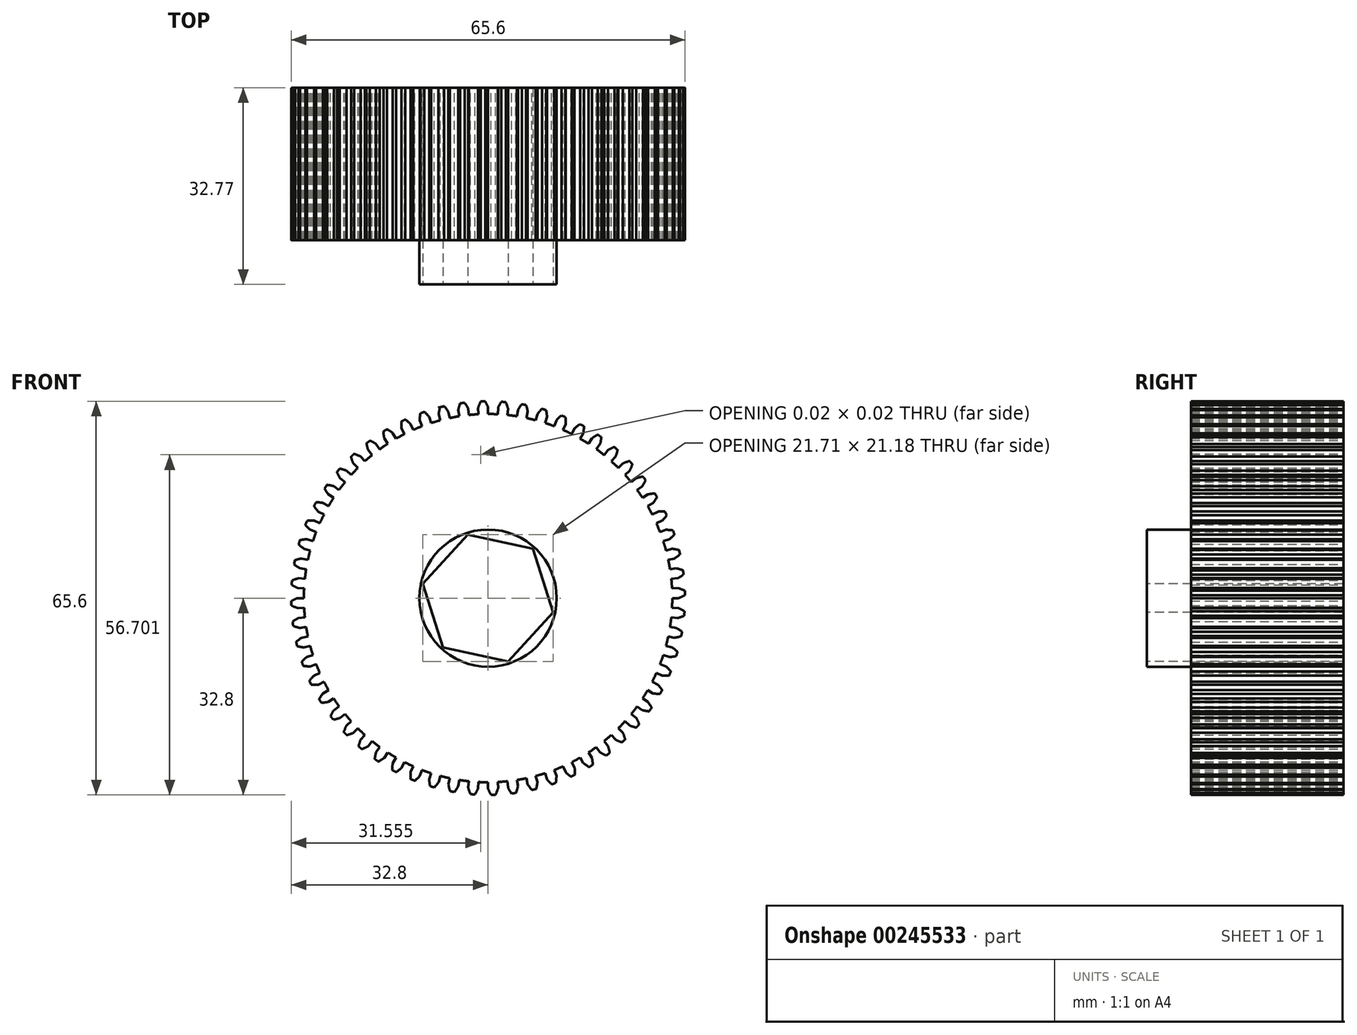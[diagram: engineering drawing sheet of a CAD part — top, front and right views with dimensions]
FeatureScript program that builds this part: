
annotation { "Feature Type Name" : "Feature", "Feature Type Description" : "" }
export const myFeature = defineFeature(function(context is Context, id is Id, definition is map)
    precondition{}
    {
        {
            var Q0;
            Q0=qCreatedBy(makeId("Front.planeOp"),FACE);
            var sketch = newSketch(context, id + "F0", { "sketchPlane" : qUnion([Q0])});
            skArc(sketch, "E0", {"start": v(-0.5, 32.8) * mm, "mid": v(-0.68, 32.8) * mm, "end": v(-0.86, 32.8) * mm});
            skLineSegment(sketch, "E1", {"start": v(0, 30.7) * mm, "end": v(0, 31.75) * mm});
            skLineSegment(sketch, "E2", {"start": v(-1.25, 23.9) * mm, "end": v(-1.25, 23.91) * mm});
            skArc(sketch, "E3", {"start": v(0, 31.75) * mm, "mid": v(-0.23, 32.28) * mm, "end": v(-0.5, 32.8) * mm});
            skArc(sketch, "E4.trimOffspring", {"start": v(-7.94, 31.83) * mm, "mid": v(-7.94, 31.79) * mm, "end": v(-7.94, 31.75) * mm});
            skArc(sketch, "E5.trimOffspring", {"start": v(-1.25, 23.91) * mm, "mid": v(-1.24, 23.91) * mm, "end": v(-1.24, 23.9) * mm});
            skLineSegment(sketch, "E6.trimOffspring", {"start": v(-0.83, 31.74) * mm, "end": v(-0.83, 31.75) * mm});
            skArc(sketch, "E7.trimOffspring", {"start": v(-1.25, 23.9) * mm, "mid": v(-1.24, 23.9) * mm, "end": v(-1.24, 23.9) * mm});
            skLineSegment(sketch, "E8.trimOffspring", {"start": v(-7.94, 31.75) * mm, "end": v(-8.25, 31.75) * mm});
            skArc(sketch, "E9.trimOffspring", {"start": v(-7.94, 31.83) * mm, "mid": v(-8.1, 31.8) * mm, "end": v(-8.25, 31.75) * mm});
            skPoint(sketch, "E10.trimOffspring.end.orphan", {"position": v(0, 60.25) * mm});
            skPoint(sketch, "E11.trimOffspring.end.orphan", {"position": v(-3.16, 60.25) * mm});
            skCircle(sketch, "E12", {"center": v(0, 0) * mm, "radius": 30.7 * mm});
            skLineSegment(sketch, "E13", {"start": v(0, 0) * mm, "end": v(-0.86, 32.8) * mm, "construction": true});
            skArc(sketch, "E14.MirrorCS", {"start": v(-1.66, 31.7) * mm, "mid": v(-1.46, 32.25) * mm, "end": v(-1.22, 32.78) * mm});
            skArc(sketch, "E15.MirrorCS", {"start": v(-1.22, 32.78) * mm, "mid": v(-1.04, 32.79) * mm, "end": v(-0.86, 32.8) * mm});
            skLineSegment(sketch, "E16.MirrorCS", {"start": v(-1.6, 30.65) * mm, "end": v(-1.66, 31.7) * mm});
            skLineSegment(sketch, "E17.1.0", {"start": v(-3.2, 30.52) * mm, "end": v(-3.32, 31.58) * mm});
            skArc(sketch, "E17.1.1", {"start": v(-3.32, 31.58) * mm, "mid": v(-3.6, 32.08) * mm, "end": v(-3.92, 32.57) * mm});
            skArc(sketch, "E17.1.2", {"start": v(-3.92, 32.57) * mm, "mid": v(-4.1, 32.55) * mm, "end": v(-4.28, 32.52) * mm});
            skArc(sketch, "E17.1.3", {"start": v(-4.64, 32.47) * mm, "mid": v(-4.46, 32.5) * mm, "end": v(-4.28, 32.52) * mm});
            skArc(sketch, "E17.1.4", {"start": v(-4.97, 31.36) * mm, "mid": v(-4.82, 31.92) * mm, "end": v(-4.64, 32.47) * mm});
            skLineSegment(sketch, "E17.1.5", {"start": v(-4.8, 30.31) * mm, "end": v(-4.97, 31.36) * mm});
            skLineSegment(sketch, "E17.2.0", {"start": v(-6.38, 30.02) * mm, "end": v(-6.6, 31.06) * mm});
            skArc(sketch, "E17.2.1", {"start": v(-6.6, 31.06) * mm, "mid": v(-6.94, 31.53) * mm, "end": v(-7.3, 31.98) * mm});
            skArc(sketch, "E17.2.2", {"start": v(-7.3, 31.98) * mm, "mid": v(-7.48, 31.94) * mm, "end": v(-7.66, 31.9) * mm});
            skArc(sketch, "E17.2.3", {"start": v(-8.01, 31.81) * mm, "mid": v(-7.83, 31.85) * mm, "end": v(-7.66, 31.9) * mm});
            skArc(sketch, "E17.2.4", {"start": v(-8.22, 30.67) * mm, "mid": v(-8.14, 31.24) * mm, "end": v(-8.01, 31.81) * mm});
            skLineSegment(sketch, "E17.2.5", {"start": v(-7.94, 29.65) * mm, "end": v(-8.22, 30.67) * mm});
            skLineSegment(sketch, "E17.3.0", {"start": v(-9.48, 29.19) * mm, "end": v(-9.81, 30.2) * mm});
            skArc(sketch, "E17.3.1", {"start": v(-9.81, 30.2) * mm, "mid": v(-10.2, 30.63) * mm, "end": v(-10.6, 31.04) * mm});
            skArc(sketch, "E17.3.2", {"start": v(-10.6, 31.04) * mm, "mid": v(-10.78, 30.98) * mm, "end": v(-10.95, 30.92) * mm});
            skArc(sketch, "E17.3.3", {"start": v(-11.3, 30.8) * mm, "mid": v(-11.12, 30.86) * mm, "end": v(-10.95, 30.92) * mm});
            skArc(sketch, "E17.3.4", {"start": v(-11.38, 29.64) * mm, "mid": v(-11.36, 30.22) * mm, "end": v(-11.3, 30.8) * mm});
            skLineSegment(sketch, "E17.3.5", {"start": v(-11, 28.65) * mm, "end": v(-11.38, 29.64) * mm});
            skLineSegment(sketch, "E17.4.0", {"start": v(-12.48, 28.04) * mm, "end": v(-12.91, 29) * mm});
            skArc(sketch, "E17.4.1", {"start": v(-12.91, 29) * mm, "mid": v(-13.34, 29.4) * mm, "end": v(-13.8, 29.76) * mm});
            skArc(sketch, "E17.4.2", {"start": v(-13.8, 29.76) * mm, "mid": v(-13.96, 29.69) * mm, "end": v(-14.12, 29.6) * mm});
            skArc(sketch, "E17.4.3", {"start": v(-14.45, 29.45) * mm, "mid": v(-14.29, 29.53) * mm, "end": v(-14.12, 29.6) * mm});
            skArc(sketch, "E17.4.4", {"start": v(-14.41, 28.29) * mm, "mid": v(-14.45, 28.87) * mm, "end": v(-14.45, 29.45) * mm});
            skLineSegment(sketch, "E17.4.5", {"start": v(-13.93, 27.35) * mm, "end": v(-14.41, 28.29) * mm});
            skLineSegment(sketch, "E17.5.0", {"start": v(-15.35, 26.58) * mm, "end": v(-15.87, 27.5) * mm});
            skArc(sketch, "E17.5.1", {"start": v(-15.88, 27.5) * mm, "mid": v(-16.34, 27.84) * mm, "end": v(-16.83, 28.16) * mm});
            skArc(sketch, "E17.5.2", {"start": v(-16.83, 28.16) * mm, "mid": v(-16.98, 28.06) * mm, "end": v(-17.14, 27.97) * mm});
            skArc(sketch, "E17.5.3", {"start": v(-17.45, 27.78) * mm, "mid": v(-17.3, 27.87) * mm, "end": v(-17.14, 27.97) * mm});
            skArc(sketch, "E17.5.4", {"start": v(-17.3, 26.63) * mm, "mid": v(-17.4, 27.2) * mm, "end": v(-17.45, 27.78) * mm});
            skLineSegment(sketch, "E17.5.5", {"start": v(-16.72, 25.74) * mm, "end": v(-17.3, 26.63) * mm});
            skLineSegment(sketch, "E17.6.0", {"start": v(-18.04, 24.83) * mm, "end": v(-18.66, 25.69) * mm});
            skArc(sketch, "E17.6.1", {"start": v(-18.66, 25.69) * mm, "mid": v(-19.16, 25.98) * mm, "end": v(-19.68, 26.25) * mm});
            skArc(sketch, "E17.6.2", {"start": v(-19.68, 26.25) * mm, "mid": v(-19.83, 26.14) * mm, "end": v(-19.97, 26.03) * mm});
            skArc(sketch, "E17.6.3", {"start": v(-20.26, 25.8) * mm, "mid": v(-20.11, 25.91) * mm, "end": v(-19.97, 26.03) * mm});
            skArc(sketch, "E17.6.4", {"start": v(-19.98, 24.67) * mm, "mid": v(-20.14, 25.23) * mm, "end": v(-20.26, 25.8) * mm});
            skLineSegment(sketch, "E17.6.5", {"start": v(-19.31, 23.85) * mm, "end": v(-19.98, 24.67) * mm});
            skLineSegment(sketch, "E17.7.0", {"start": v(-20.54, 22.8) * mm, "end": v(-21.24, 23.6) * mm});
            skArc(sketch, "E17.7.1", {"start": v(-21.24, 23.6) * mm, "mid": v(-21.77, 23.84) * mm, "end": v(-22.32, 24.04) * mm});
            skArc(sketch, "E17.7.2", {"start": v(-22.32, 24.04) * mm, "mid": v(-22.45, 23.92) * mm, "end": v(-22.58, 23.8) * mm});
            skArc(sketch, "E17.7.3", {"start": v(-22.84, 23.54) * mm, "mid": v(-22.71, 23.67) * mm, "end": v(-22.58, 23.8) * mm});
            skArc(sketch, "E17.7.4", {"start": v(-22.45, 22.45) * mm, "mid": v(-22.67, 22.99) * mm, "end": v(-22.84, 23.54) * mm});
            skLineSegment(sketch, "E17.7.5", {"start": v(-21.7, 21.7) * mm, "end": v(-22.45, 22.45) * mm});
            skLineSegment(sketch, "E17.8.0", {"start": v(-22.8, 20.54) * mm, "end": v(-23.6, 21.24) * mm});
            skArc(sketch, "E17.8.1", {"start": v(-23.6, 21.24) * mm, "mid": v(-24.14, 21.43) * mm, "end": v(-24.7, 21.58) * mm});
            skArc(sketch, "E17.8.2", {"start": v(-24.7, 21.58) * mm, "mid": v(-24.83, 21.44) * mm, "end": v(-24.94, 21.3) * mm});
            skArc(sketch, "E17.8.3", {"start": v(-25.18, 21.03) * mm, "mid": v(-25.06, 21.17) * mm, "end": v(-24.94, 21.3) * mm});
            skArc(sketch, "E17.8.4", {"start": v(-24.67, 19.98) * mm, "mid": v(-24.95, 20.5) * mm, "end": v(-25.18, 21.03) * mm});
            skLineSegment(sketch, "E17.8.5", {"start": v(-23.85, 19.31) * mm, "end": v(-24.67, 19.98) * mm});
            skLineSegment(sketch, "E17.9.0", {"start": v(-24.83, 18.04) * mm, "end": v(-25.69, 18.66) * mm});
            skArc(sketch, "E17.9.1", {"start": v(-25.69, 18.66) * mm, "mid": v(-26.25, 18.8) * mm, "end": v(-26.83, 18.88) * mm});
            skArc(sketch, "E17.9.2", {"start": v(-26.83, 18.88) * mm, "mid": v(-26.93, 18.73) * mm, "end": v(-27.03, 18.58) * mm});
            skArc(sketch, "E17.9.3", {"start": v(-27.24, 18.28) * mm, "mid": v(-27.14, 18.43) * mm, "end": v(-27.03, 18.58) * mm});
            skArc(sketch, "E17.9.4", {"start": v(-26.63, 17.3) * mm, "mid": v(-26.95, 17.77) * mm, "end": v(-27.24, 18.28) * mm});
            skLineSegment(sketch, "E17.9.5", {"start": v(-25.74, 16.72) * mm, "end": v(-26.63, 17.3) * mm});
            skLineSegment(sketch, "E17.10.0", {"start": v(-26.58, 15.35) * mm, "end": v(-27.5, 15.88) * mm});
            skArc(sketch, "E17.10.1", {"start": v(-27.5, 15.88) * mm, "mid": v(-28.07, 15.94) * mm, "end": v(-28.65, 15.97) * mm});
            skArc(sketch, "E17.10.2", {"start": v(-28.65, 15.97) * mm, "mid": v(-28.74, 15.81) * mm, "end": v(-28.83, 15.65) * mm});
            skArc(sketch, "E17.10.3", {"start": v(-29, 15.33) * mm, "mid": v(-28.92, 15.5) * mm, "end": v(-28.83, 15.65) * mm});
            skArc(sketch, "E17.10.4", {"start": v(-28.29, 14.41) * mm, "mid": v(-28.66, 14.86) * mm, "end": v(-29, 15.33) * mm});
            skLineSegment(sketch, "E17.10.5", {"start": v(-27.35, 13.93) * mm, "end": v(-28.29, 14.41) * mm});
            skLineSegment(sketch, "E17.11.0", {"start": v(-28.04, 12.48) * mm, "end": v(-29, 12.91) * mm});
            skArc(sketch, "E17.11.1", {"start": v(-29, 12.91) * mm, "mid": v(-29.59, 12.92) * mm, "end": v(-30.17, 12.89) * mm});
            skArc(sketch, "E17.11.2", {"start": v(-30.17, 12.89) * mm, "mid": v(-30.24, 12.72) * mm, "end": v(-30.3, 12.55) * mm});
            skArc(sketch, "E17.11.3", {"start": v(-30.44, 12.22) * mm, "mid": v(-30.38, 12.39) * mm, "end": v(-30.3, 12.55) * mm});
            skArc(sketch, "E17.11.4", {"start": v(-29.64, 11.38) * mm, "mid": v(-30.06, 11.78) * mm, "end": v(-30.44, 12.22) * mm});
            skLineSegment(sketch, "E17.11.5", {"start": v(-28.65, 11) * mm, "end": v(-29.64, 11.38) * mm});
            skLineSegment(sketch, "E17.12.0", {"start": v(-29.19, 9.48) * mm, "end": v(-30.2, 9.81) * mm});
            skArc(sketch, "E17.12.1", {"start": v(-30.2, 9.81) * mm, "mid": v(-30.77, 9.76) * mm, "end": v(-31.35, 9.67) * mm});
            skArc(sketch, "E17.12.2", {"start": v(-31.35, 9.67) * mm, "mid": v(-31.4, 9.5) * mm, "end": v(-31.45, 9.32) * mm});
            skArc(sketch, "E17.12.3", {"start": v(-31.55, 8.97) * mm, "mid": v(-31.5, 9.14) * mm, "end": v(-31.45, 9.32) * mm});
            skArc(sketch, "E17.12.4", {"start": v(-30.67, 8.22) * mm, "mid": v(-31.13, 8.58) * mm, "end": v(-31.55, 8.97) * mm});
            skLineSegment(sketch, "E17.12.5", {"start": v(-29.65, 7.94) * mm, "end": v(-30.67, 8.22) * mm});
            skLineSegment(sketch, "E17.13.0", {"start": v(-30.02, 6.38) * mm, "end": v(-31.06, 6.6) * mm});
            skArc(sketch, "E17.13.1", {"start": v(-31.06, 6.6) * mm, "mid": v(-31.63, 6.49) * mm, "end": v(-32.19, 6.34) * mm});
            skArc(sketch, "E17.13.2", {"start": v(-32.19, 6.34) * mm, "mid": v(-32.22, 6.16) * mm, "end": v(-32.25, 5.98) * mm});
            skArc(sketch, "E17.13.3", {"start": v(-32.32, 5.62) * mm, "mid": v(-32.29, 5.8) * mm, "end": v(-32.25, 5.98) * mm});
            skArc(sketch, "E17.13.4", {"start": v(-31.36, 4.97) * mm, "mid": v(-31.85, 5.28) * mm, "end": v(-32.32, 5.62) * mm});
            skLineSegment(sketch, "E17.13.5", {"start": v(-30.31, 4.8) * mm, "end": v(-31.36, 4.97) * mm});
            skLineSegment(sketch, "E17.14.0", {"start": v(-30.52, 3.2) * mm, "end": v(-31.58, 3.32) * mm});
            skArc(sketch, "E17.14.1", {"start": v(-31.58, 3.32) * mm, "mid": v(-32.13, 3.15) * mm, "end": v(-32.67, 2.94) * mm});
            skArc(sketch, "E17.14.2", {"start": v(-32.67, 2.94) * mm, "mid": v(-32.69, 2.76) * mm, "end": v(-32.7, 2.57) * mm});
            skArc(sketch, "E17.14.3", {"start": v(-32.73, 2.21) * mm, "mid": v(-32.72, 2.4) * mm, "end": v(-32.7, 2.57) * mm});
            skArc(sketch, "E17.14.4", {"start": v(-31.7, 1.66) * mm, "mid": v(-32.23, 1.92) * mm, "end": v(-32.73, 2.21) * mm});
            skLineSegment(sketch, "E17.14.5", {"start": v(-30.65, 1.6) * mm, "end": v(-31.7, 1.66) * mm});
            skLineSegment(sketch, "E17.15.0", {"start": v(-30.7, 0) * mm, "end": v(-31.75, 0) * mm});
            skArc(sketch, "E17.15.1", {"start": v(-31.75, 0) * mm, "mid": v(-32.28, -0.23) * mm, "end": v(-32.8, -0.5) * mm});
            skArc(sketch, "E17.15.2", {"start": v(-32.8, -0.5) * mm, "mid": v(-32.8, -0.68) * mm, "end": v(-32.8, -0.86) * mm});
            skArc(sketch, "E17.15.3", {"start": v(-32.78, -1.22) * mm, "mid": v(-32.79, -1.04) * mm, "end": v(-32.8, -0.86) * mm});
            skArc(sketch, "E17.15.4", {"start": v(-31.7, -1.66) * mm, "mid": v(-32.25, -1.46) * mm, "end": v(-32.78, -1.22) * mm});
            skLineSegment(sketch, "E17.15.5", {"start": v(-30.65, -1.6) * mm, "end": v(-31.7, -1.66) * mm});
            skLineSegment(sketch, "E17.16.0", {"start": v(-30.52, -3.2) * mm, "end": v(-31.58, -3.32) * mm});
            skArc(sketch, "E17.16.1", {"start": v(-31.58, -3.32) * mm, "mid": v(-32.08, -3.6) * mm, "end": v(-32.57, -3.92) * mm});
            skArc(sketch, "E17.16.2", {"start": v(-32.57, -3.92) * mm, "mid": v(-32.55, -4.1) * mm, "end": v(-32.52, -4.28) * mm});
            skArc(sketch, "E17.16.3", {"start": v(-32.47, -4.64) * mm, "mid": v(-32.5, -4.46) * mm, "end": v(-32.52, -4.28) * mm});
            skArc(sketch, "E17.16.4", {"start": v(-31.36, -4.97) * mm, "mid": v(-31.92, -4.82) * mm, "end": v(-32.47, -4.64) * mm});
            skLineSegment(sketch, "E17.16.5", {"start": v(-30.31, -4.8) * mm, "end": v(-31.36, -4.97) * mm});
            skLineSegment(sketch, "E17.17.0", {"start": v(-30.02, -6.38) * mm, "end": v(-31.06, -6.6) * mm});
            skArc(sketch, "E17.17.1", {"start": v(-31.06, -6.6) * mm, "mid": v(-31.53, -6.94) * mm, "end": v(-31.98, -7.3) * mm});
            skArc(sketch, "E17.17.2", {"start": v(-31.98, -7.3) * mm, "mid": v(-31.94, -7.48) * mm, "end": v(-31.9, -7.66) * mm});
            skArc(sketch, "E17.17.3", {"start": v(-31.81, -8.01) * mm, "mid": v(-31.85, -7.83) * mm, "end": v(-31.9, -7.66) * mm});
            skArc(sketch, "E17.17.4", {"start": v(-30.67, -8.22) * mm, "mid": v(-31.24, -8.14) * mm, "end": v(-31.81, -8.01) * mm});
            skLineSegment(sketch, "E17.17.5", {"start": v(-29.65, -7.94) * mm, "end": v(-30.67, -8.22) * mm});
            skLineSegment(sketch, "E17.18.0", {"start": v(-29.19, -9.48) * mm, "end": v(-30.2, -9.81) * mm});
            skArc(sketch, "E17.18.1", {"start": v(-30.2, -9.81) * mm, "mid": v(-30.63, -10.2) * mm, "end": v(-31.04, -10.6) * mm});
            skArc(sketch, "E17.18.2", {"start": v(-31.04, -10.6) * mm, "mid": v(-30.98, -10.78) * mm, "end": v(-30.92, -10.95) * mm});
            skArc(sketch, "E17.18.3", {"start": v(-30.8, -11.3) * mm, "mid": v(-30.86, -11.12) * mm, "end": v(-30.92, -10.95) * mm});
            skArc(sketch, "E17.18.4", {"start": v(-29.64, -11.38) * mm, "mid": v(-30.22, -11.36) * mm, "end": v(-30.8, -11.3) * mm});
            skLineSegment(sketch, "E17.18.5", {"start": v(-28.65, -11) * mm, "end": v(-29.64, -11.38) * mm});
            skLineSegment(sketch, "E17.19.0", {"start": v(-28.04, -12.48) * mm, "end": v(-29, -12.91) * mm});
            skArc(sketch, "E17.19.1", {"start": v(-29, -12.91) * mm, "mid": v(-29.4, -13.34) * mm, "end": v(-29.76, -13.8) * mm});
            skArc(sketch, "E17.19.2", {"start": v(-29.76, -13.8) * mm, "mid": v(-29.69, -13.96) * mm, "end": v(-29.6, -14.12) * mm});
            skArc(sketch, "E17.19.3", {"start": v(-29.45, -14.45) * mm, "mid": v(-29.53, -14.29) * mm, "end": v(-29.6, -14.12) * mm});
            skArc(sketch, "E17.19.4", {"start": v(-28.29, -14.41) * mm, "mid": v(-28.87, -14.45) * mm, "end": v(-29.45, -14.45) * mm});
            skLineSegment(sketch, "E17.19.5", {"start": v(-27.35, -13.93) * mm, "end": v(-28.29, -14.41) * mm});
            skLineSegment(sketch, "E17.20.0", {"start": v(-26.58, -15.35) * mm, "end": v(-27.5, -15.87) * mm});
            skArc(sketch, "E17.20.1", {"start": v(-27.5, -15.87) * mm, "mid": v(-27.84, -16.34) * mm, "end": v(-28.16, -16.83) * mm});
            skArc(sketch, "E17.20.2", {"start": v(-28.16, -16.83) * mm, "mid": v(-28.06, -16.98) * mm, "end": v(-27.97, -17.14) * mm});
            skArc(sketch, "E17.20.3", {"start": v(-27.78, -17.45) * mm, "mid": v(-27.87, -17.3) * mm, "end": v(-27.97, -17.14) * mm});
            skArc(sketch, "E17.20.4", {"start": v(-26.63, -17.3) * mm, "mid": v(-27.2, -17.4) * mm, "end": v(-27.78, -17.45) * mm});
            skLineSegment(sketch, "E17.20.5", {"start": v(-25.74, -16.72) * mm, "end": v(-26.63, -17.3) * mm});
            skLineSegment(sketch, "E17.21.0", {"start": v(-24.83, -18.04) * mm, "end": v(-25.69, -18.66) * mm});
            skArc(sketch, "E17.21.1", {"start": v(-25.69, -18.66) * mm, "mid": v(-25.98, -19.16) * mm, "end": v(-26.25, -19.68) * mm});
            skArc(sketch, "E17.21.2", {"start": v(-26.25, -19.68) * mm, "mid": v(-26.14, -19.83) * mm, "end": v(-26.03, -19.97) * mm});
            skArc(sketch, "E17.21.3", {"start": v(-25.8, -20.26) * mm, "mid": v(-25.91, -20.11) * mm, "end": v(-26.03, -19.97) * mm});
            skArc(sketch, "E17.21.4", {"start": v(-24.67, -19.98) * mm, "mid": v(-25.23, -20.14) * mm, "end": v(-25.8, -20.26) * mm});
            skLineSegment(sketch, "E17.21.5", {"start": v(-23.85, -19.31) * mm, "end": v(-24.67, -19.98) * mm});
            skLineSegment(sketch, "E17.22.0", {"start": v(-22.8, -20.54) * mm, "end": v(-23.6, -21.24) * mm});
            skArc(sketch, "E17.22.1", {"start": v(-23.6, -21.24) * mm, "mid": v(-23.84, -21.77) * mm, "end": v(-24.04, -22.32) * mm});
            skArc(sketch, "E17.22.2", {"start": v(-24.04, -22.32) * mm, "mid": v(-23.92, -22.45) * mm, "end": v(-23.8, -22.58) * mm});
            skArc(sketch, "E17.22.3", {"start": v(-23.54, -22.84) * mm, "mid": v(-23.67, -22.71) * mm, "end": v(-23.8, -22.58) * mm});
            skArc(sketch, "E17.22.4", {"start": v(-22.45, -22.45) * mm, "mid": v(-22.99, -22.67) * mm, "end": v(-23.54, -22.84) * mm});
            skLineSegment(sketch, "E17.22.5", {"start": v(-21.7, -21.7) * mm, "end": v(-22.45, -22.45) * mm});
            skLineSegment(sketch, "E17.23.0", {"start": v(-20.54, -22.8) * mm, "end": v(-21.24, -23.6) * mm});
            skArc(sketch, "E17.23.1", {"start": v(-21.24, -23.6) * mm, "mid": v(-21.43, -24.14) * mm, "end": v(-21.58, -24.7) * mm});
            skArc(sketch, "E17.23.2", {"start": v(-21.58, -24.7) * mm, "mid": v(-21.44, -24.83) * mm, "end": v(-21.3, -24.94) * mm});
            skArc(sketch, "E17.23.3", {"start": v(-21.03, -25.18) * mm, "mid": v(-21.17, -25.06) * mm, "end": v(-21.3, -24.94) * mm});
            skArc(sketch, "E17.23.4", {"start": v(-19.98, -24.67) * mm, "mid": v(-20.5, -24.95) * mm, "end": v(-21.03, -25.18) * mm});
            skLineSegment(sketch, "E17.23.5", {"start": v(-19.31, -23.85) * mm, "end": v(-19.98, -24.67) * mm});
            skLineSegment(sketch, "E17.24.0", {"start": v(-18.04, -24.83) * mm, "end": v(-18.66, -25.69) * mm});
            skArc(sketch, "E17.24.1", {"start": v(-18.66, -25.69) * mm, "mid": v(-18.8, -26.25) * mm, "end": v(-18.88, -26.83) * mm});
            skArc(sketch, "E17.24.2", {"start": v(-18.88, -26.83) * mm, "mid": v(-18.73, -26.93) * mm, "end": v(-18.58, -27.03) * mm});
            skArc(sketch, "E17.24.3", {"start": v(-18.28, -27.24) * mm, "mid": v(-18.43, -27.14) * mm, "end": v(-18.58, -27.03) * mm});
            skArc(sketch, "E17.24.4", {"start": v(-17.3, -26.63) * mm, "mid": v(-17.77, -26.95) * mm, "end": v(-18.28, -27.24) * mm});
            skLineSegment(sketch, "E17.24.5", {"start": v(-16.72, -25.74) * mm, "end": v(-17.3, -26.63) * mm});
            skLineSegment(sketch, "E17.25.0", {"start": v(-15.35, -26.58) * mm, "end": v(-15.87, -27.5) * mm});
            skArc(sketch, "E17.25.1", {"start": v(-15.87, -27.5) * mm, "mid": v(-15.94, -28.07) * mm, "end": v(-15.97, -28.65) * mm});
            skArc(sketch, "E17.25.2", {"start": v(-15.97, -28.65) * mm, "mid": v(-15.81, -28.74) * mm, "end": v(-15.65, -28.83) * mm});
            skArc(sketch, "E17.25.3", {"start": v(-15.33, -29) * mm, "mid": v(-15.5, -28.92) * mm, "end": v(-15.65, -28.83) * mm});
            skArc(sketch, "E17.25.4", {"start": v(-14.41, -28.29) * mm, "mid": v(-14.86, -28.66) * mm, "end": v(-15.33, -29) * mm});
            skLineSegment(sketch, "E17.25.5", {"start": v(-13.93, -27.35) * mm, "end": v(-14.41, -28.29) * mm});
            skLineSegment(sketch, "E17.26.0", {"start": v(-12.48, -28.04) * mm, "end": v(-12.91, -29) * mm});
            skArc(sketch, "E17.26.1", {"start": v(-12.91, -29) * mm, "mid": v(-12.92, -29.59) * mm, "end": v(-12.89, -30.17) * mm});
            skArc(sketch, "E17.26.2", {"start": v(-12.89, -30.17) * mm, "mid": v(-12.72, -30.24) * mm, "end": v(-12.55, -30.3) * mm});
            skArc(sketch, "E17.26.3", {"start": v(-12.22, -30.44) * mm, "mid": v(-12.39, -30.38) * mm, "end": v(-12.55, -30.3) * mm});
            skArc(sketch, "E17.26.4", {"start": v(-11.38, -29.64) * mm, "mid": v(-11.78, -30.06) * mm, "end": v(-12.22, -30.44) * mm});
            skLineSegment(sketch, "E17.26.5", {"start": v(-11, -28.65) * mm, "end": v(-11.38, -29.64) * mm});
            skLineSegment(sketch, "E17.27.0", {"start": v(-9.48, -29.19) * mm, "end": v(-9.81, -30.2) * mm});
            skArc(sketch, "E17.27.1", {"start": v(-9.81, -30.2) * mm, "mid": v(-9.76, -30.77) * mm, "end": v(-9.67, -31.35) * mm});
            skArc(sketch, "E17.27.2", {"start": v(-9.67, -31.35) * mm, "mid": v(-9.5, -31.4) * mm, "end": v(-9.32, -31.45) * mm});
            skArc(sketch, "E17.27.3", {"start": v(-8.97, -31.55) * mm, "mid": v(-9.14, -31.5) * mm, "end": v(-9.32, -31.45) * mm});
            skArc(sketch, "E17.27.4", {"start": v(-8.22, -30.67) * mm, "mid": v(-8.58, -31.13) * mm, "end": v(-8.97, -31.55) * mm});
            skLineSegment(sketch, "E17.27.5", {"start": v(-7.94, -29.65) * mm, "end": v(-8.22, -30.67) * mm});
            skLineSegment(sketch, "E17.28.0", {"start": v(-6.38, -30.02) * mm, "end": v(-6.6, -31.06) * mm});
            skArc(sketch, "E17.28.1", {"start": v(-6.6, -31.06) * mm, "mid": v(-6.49, -31.63) * mm, "end": v(-6.34, -32.19) * mm});
            skArc(sketch, "E17.28.2", {"start": v(-6.34, -32.19) * mm, "mid": v(-6.16, -32.22) * mm, "end": v(-5.98, -32.25) * mm});
            skArc(sketch, "E17.28.3", {"start": v(-5.62, -32.32) * mm, "mid": v(-5.8, -32.29) * mm, "end": v(-5.98, -32.25) * mm});
            skArc(sketch, "E17.28.4", {"start": v(-4.97, -31.36) * mm, "mid": v(-5.28, -31.85) * mm, "end": v(-5.62, -32.32) * mm});
            skLineSegment(sketch, "E17.28.5", {"start": v(-4.8, -30.31) * mm, "end": v(-4.97, -31.36) * mm});
            skLineSegment(sketch, "E17.29.0", {"start": v(-3.2, -30.52) * mm, "end": v(-3.32, -31.58) * mm});
            skArc(sketch, "E17.29.1", {"start": v(-3.32, -31.58) * mm, "mid": v(-3.15, -32.13) * mm, "end": v(-2.94, -32.67) * mm});
            skArc(sketch, "E17.29.2", {"start": v(-2.94, -32.67) * mm, "mid": v(-2.76, -32.69) * mm, "end": v(-2.57, -32.7) * mm});
            skArc(sketch, "E17.29.3", {"start": v(-2.21, -32.73) * mm, "mid": v(-2.4, -32.72) * mm, "end": v(-2.57, -32.7) * mm});
            skArc(sketch, "E17.29.4", {"start": v(-1.66, -31.7) * mm, "mid": v(-1.92, -32.23) * mm, "end": v(-2.21, -32.73) * mm});
            skLineSegment(sketch, "E17.29.5", {"start": v(-1.6, -30.65) * mm, "end": v(-1.66, -31.7) * mm});
            skLineSegment(sketch, "E17.30.0", {"start": v(0, -30.7) * mm, "end": v(0, -31.75) * mm});
            skArc(sketch, "E17.30.1", {"start": v(0, -31.75) * mm, "mid": v(0.23, -32.28) * mm, "end": v(0.5, -32.8) * mm});
            skArc(sketch, "E17.30.2", {"start": v(0.5, -32.8) * mm, "mid": v(0.68, -32.8) * mm, "end": v(0.86, -32.8) * mm});
            skArc(sketch, "E17.30.3", {"start": v(1.22, -32.78) * mm, "mid": v(1.04, -32.79) * mm, "end": v(0.86, -32.8) * mm});
            skArc(sketch, "E17.30.4", {"start": v(1.66, -31.7) * mm, "mid": v(1.46, -32.25) * mm, "end": v(1.22, -32.78) * mm});
            skLineSegment(sketch, "E17.30.5", {"start": v(1.6, -30.65) * mm, "end": v(1.66, -31.7) * mm});
            skLineSegment(sketch, "E17.31.0", {"start": v(3.2, -30.52) * mm, "end": v(3.32, -31.58) * mm});
            skArc(sketch, "E17.31.1", {"start": v(3.32, -31.58) * mm, "mid": v(3.6, -32.08) * mm, "end": v(3.92, -32.57) * mm});
            skArc(sketch, "E17.31.2", {"start": v(3.92, -32.57) * mm, "mid": v(4.1, -32.55) * mm, "end": v(4.28, -32.52) * mm});
            skArc(sketch, "E17.31.3", {"start": v(4.64, -32.47) * mm, "mid": v(4.46, -32.5) * mm, "end": v(4.28, -32.52) * mm});
            skArc(sketch, "E17.31.4", {"start": v(4.97, -31.36) * mm, "mid": v(4.82, -31.92) * mm, "end": v(4.64, -32.47) * mm});
            skLineSegment(sketch, "E17.31.5", {"start": v(4.8, -30.31) * mm, "end": v(4.97, -31.36) * mm});
            skLineSegment(sketch, "E17.32.0", {"start": v(6.38, -30.02) * mm, "end": v(6.6, -31.06) * mm});
            skArc(sketch, "E17.32.1", {"start": v(6.6, -31.06) * mm, "mid": v(6.94, -31.53) * mm, "end": v(7.3, -31.98) * mm});
            skArc(sketch, "E17.32.2", {"start": v(7.3, -31.98) * mm, "mid": v(7.48, -31.94) * mm, "end": v(7.66, -31.9) * mm});
            skArc(sketch, "E17.32.3", {"start": v(8.01, -31.81) * mm, "mid": v(7.83, -31.85) * mm, "end": v(7.66, -31.9) * mm});
            skArc(sketch, "E17.32.4", {"start": v(8.22, -30.67) * mm, "mid": v(8.14, -31.24) * mm, "end": v(8.01, -31.81) * mm});
            skLineSegment(sketch, "E17.32.5", {"start": v(7.94, -29.65) * mm, "end": v(8.22, -30.67) * mm});
            skLineSegment(sketch, "E17.33.0", {"start": v(9.48, -29.19) * mm, "end": v(9.81, -30.2) * mm});
            skArc(sketch, "E17.33.1", {"start": v(9.81, -30.2) * mm, "mid": v(10.2, -30.63) * mm, "end": v(10.6, -31.04) * mm});
            skArc(sketch, "E17.33.2", {"start": v(10.6, -31.04) * mm, "mid": v(10.78, -30.98) * mm, "end": v(10.95, -30.92) * mm});
            skArc(sketch, "E17.33.3", {"start": v(11.3, -30.8) * mm, "mid": v(11.12, -30.86) * mm, "end": v(10.95, -30.92) * mm});
            skArc(sketch, "E17.33.4", {"start": v(11.38, -29.64) * mm, "mid": v(11.36, -30.22) * mm, "end": v(11.3, -30.8) * mm});
            skLineSegment(sketch, "E17.33.5", {"start": v(11, -28.65) * mm, "end": v(11.38, -29.64) * mm});
            skLineSegment(sketch, "E17.34.0", {"start": v(12.48, -28.04) * mm, "end": v(12.91, -29) * mm});
            skArc(sketch, "E17.34.1", {"start": v(12.91, -29) * mm, "mid": v(13.34, -29.4) * mm, "end": v(13.8, -29.76) * mm});
            skArc(sketch, "E17.34.2", {"start": v(13.8, -29.76) * mm, "mid": v(13.96, -29.69) * mm, "end": v(14.12, -29.6) * mm});
            skArc(sketch, "E17.34.3", {"start": v(14.45, -29.45) * mm, "mid": v(14.29, -29.53) * mm, "end": v(14.12, -29.6) * mm});
            skArc(sketch, "E17.34.4", {"start": v(14.41, -28.29) * mm, "mid": v(14.45, -28.87) * mm, "end": v(14.45, -29.45) * mm});
            skLineSegment(sketch, "E17.34.5", {"start": v(13.93, -27.35) * mm, "end": v(14.41, -28.29) * mm});
            skLineSegment(sketch, "E17.35.0", {"start": v(15.35, -26.58) * mm, "end": v(15.87, -27.5) * mm});
            skArc(sketch, "E17.35.1", {"start": v(15.87, -27.5) * mm, "mid": v(16.34, -27.84) * mm, "end": v(16.83, -28.16) * mm});
            skArc(sketch, "E17.35.2", {"start": v(16.83, -28.16) * mm, "mid": v(16.98, -28.06) * mm, "end": v(17.14, -27.97) * mm});
            skArc(sketch, "E17.35.3", {"start": v(17.45, -27.78) * mm, "mid": v(17.3, -27.87) * mm, "end": v(17.14, -27.97) * mm});
            skArc(sketch, "E17.35.4", {"start": v(17.3, -26.63) * mm, "mid": v(17.4, -27.2) * mm, "end": v(17.45, -27.78) * mm});
            skLineSegment(sketch, "E17.35.5", {"start": v(16.72, -25.74) * mm, "end": v(17.3, -26.63) * mm});
            skLineSegment(sketch, "E17.36.0", {"start": v(18.04, -24.83) * mm, "end": v(18.66, -25.69) * mm});
            skArc(sketch, "E17.36.1", {"start": v(18.66, -25.69) * mm, "mid": v(19.16, -25.98) * mm, "end": v(19.68, -26.25) * mm});
            skArc(sketch, "E17.36.2", {"start": v(19.68, -26.25) * mm, "mid": v(19.83, -26.14) * mm, "end": v(19.97, -26.03) * mm});
            skArc(sketch, "E17.36.3", {"start": v(20.26, -25.8) * mm, "mid": v(20.11, -25.91) * mm, "end": v(19.97, -26.03) * mm});
            skArc(sketch, "E17.36.4", {"start": v(19.98, -24.67) * mm, "mid": v(20.14, -25.23) * mm, "end": v(20.26, -25.8) * mm});
            skLineSegment(sketch, "E17.36.5", {"start": v(19.31, -23.85) * mm, "end": v(19.98, -24.67) * mm});
            skLineSegment(sketch, "E17.37.0", {"start": v(20.54, -22.8) * mm, "end": v(21.24, -23.6) * mm});
            skArc(sketch, "E17.37.1", {"start": v(21.24, -23.6) * mm, "mid": v(21.77, -23.84) * mm, "end": v(22.32, -24.04) * mm});
            skArc(sketch, "E17.37.2", {"start": v(22.32, -24.04) * mm, "mid": v(22.45, -23.92) * mm, "end": v(22.58, -23.8) * mm});
            skArc(sketch, "E17.37.3", {"start": v(22.84, -23.54) * mm, "mid": v(22.71, -23.67) * mm, "end": v(22.58, -23.8) * mm});
            skArc(sketch, "E17.37.4", {"start": v(22.45, -22.45) * mm, "mid": v(22.67, -22.99) * mm, "end": v(22.84, -23.54) * mm});
            skLineSegment(sketch, "E17.37.5", {"start": v(21.7, -21.7) * mm, "end": v(22.45, -22.45) * mm});
            skLineSegment(sketch, "E17.38.0", {"start": v(22.8, -20.54) * mm, "end": v(23.6, -21.24) * mm});
            skArc(sketch, "E17.38.1", {"start": v(23.6, -21.24) * mm, "mid": v(24.14, -21.43) * mm, "end": v(24.7, -21.58) * mm});
            skArc(sketch, "E17.38.2", {"start": v(24.7, -21.58) * mm, "mid": v(24.83, -21.44) * mm, "end": v(24.94, -21.3) * mm});
            skArc(sketch, "E17.38.3", {"start": v(25.18, -21.03) * mm, "mid": v(25.06, -21.17) * mm, "end": v(24.94, -21.3) * mm});
            skArc(sketch, "E17.38.4", {"start": v(24.67, -19.98) * mm, "mid": v(24.95, -20.5) * mm, "end": v(25.18, -21.03) * mm});
            skLineSegment(sketch, "E17.38.5", {"start": v(23.85, -19.31) * mm, "end": v(24.67, -19.98) * mm});
            skLineSegment(sketch, "E17.39.0", {"start": v(24.83, -18.04) * mm, "end": v(25.69, -18.66) * mm});
            skArc(sketch, "E17.39.1", {"start": v(25.69, -18.66) * mm, "mid": v(26.25, -18.8) * mm, "end": v(26.83, -18.88) * mm});
            skArc(sketch, "E17.39.2", {"start": v(26.83, -18.88) * mm, "mid": v(26.93, -18.73) * mm, "end": v(27.03, -18.58) * mm});
            skArc(sketch, "E17.39.3", {"start": v(27.24, -18.28) * mm, "mid": v(27.14, -18.43) * mm, "end": v(27.03, -18.58) * mm});
            skArc(sketch, "E17.39.4", {"start": v(26.63, -17.3) * mm, "mid": v(26.95, -17.77) * mm, "end": v(27.24, -18.28) * mm});
            skLineSegment(sketch, "E17.39.5", {"start": v(25.74, -16.72) * mm, "end": v(26.63, -17.3) * mm});
            skLineSegment(sketch, "E17.40.0", {"start": v(26.58, -15.35) * mm, "end": v(27.5, -15.88) * mm});
            skArc(sketch, "E17.40.1", {"start": v(27.5, -15.88) * mm, "mid": v(28.07, -15.94) * mm, "end": v(28.65, -15.97) * mm});
            skArc(sketch, "E17.40.2", {"start": v(28.65, -15.97) * mm, "mid": v(28.74, -15.81) * mm, "end": v(28.83, -15.65) * mm});
            skArc(sketch, "E17.40.3", {"start": v(29, -15.33) * mm, "mid": v(28.92, -15.5) * mm, "end": v(28.83, -15.65) * mm});
            skArc(sketch, "E17.40.4", {"start": v(28.29, -14.41) * mm, "mid": v(28.66, -14.86) * mm, "end": v(29, -15.33) * mm});
            skLineSegment(sketch, "E17.40.5", {"start": v(27.35, -13.93) * mm, "end": v(28.29, -14.41) * mm});
            skLineSegment(sketch, "E17.41.0", {"start": v(28.04, -12.48) * mm, "end": v(29, -12.91) * mm});
            skArc(sketch, "E17.41.1", {"start": v(29, -12.91) * mm, "mid": v(29.59, -12.92) * mm, "end": v(30.17, -12.89) * mm});
            skArc(sketch, "E17.41.2", {"start": v(30.17, -12.89) * mm, "mid": v(30.24, -12.72) * mm, "end": v(30.3, -12.55) * mm});
            skArc(sketch, "E17.41.3", {"start": v(30.44, -12.22) * mm, "mid": v(30.38, -12.39) * mm, "end": v(30.3, -12.55) * mm});
            skArc(sketch, "E17.41.4", {"start": v(29.64, -11.38) * mm, "mid": v(30.06, -11.78) * mm, "end": v(30.44, -12.22) * mm});
            skLineSegment(sketch, "E17.41.5", {"start": v(28.65, -11) * mm, "end": v(29.64, -11.38) * mm});
            skLineSegment(sketch, "E17.42.0", {"start": v(29.19, -9.48) * mm, "end": v(30.2, -9.81) * mm});
            skArc(sketch, "E17.42.1", {"start": v(30.2, -9.81) * mm, "mid": v(30.77, -9.76) * mm, "end": v(31.35, -9.67) * mm});
            skArc(sketch, "E17.42.2", {"start": v(31.35, -9.67) * mm, "mid": v(31.4, -9.5) * mm, "end": v(31.45, -9.32) * mm});
            skArc(sketch, "E17.42.3", {"start": v(31.55, -8.97) * mm, "mid": v(31.5, -9.14) * mm, "end": v(31.45, -9.32) * mm});
            skArc(sketch, "E17.42.4", {"start": v(30.67, -8.22) * mm, "mid": v(31.13, -8.58) * mm, "end": v(31.55, -8.97) * mm});
            skLineSegment(sketch, "E17.42.5", {"start": v(29.65, -7.94) * mm, "end": v(30.67, -8.22) * mm});
            skLineSegment(sketch, "E17.43.0", {"start": v(30.02, -6.38) * mm, "end": v(31.06, -6.6) * mm});
            skArc(sketch, "E17.43.1", {"start": v(31.06, -6.6) * mm, "mid": v(31.63, -6.49) * mm, "end": v(32.19, -6.34) * mm});
            skArc(sketch, "E17.43.2", {"start": v(32.19, -6.34) * mm, "mid": v(32.22, -6.16) * mm, "end": v(32.25, -5.98) * mm});
            skArc(sketch, "E17.43.3", {"start": v(32.32, -5.62) * mm, "mid": v(32.29, -5.8) * mm, "end": v(32.25, -5.98) * mm});
            skArc(sketch, "E17.43.4", {"start": v(31.36, -4.97) * mm, "mid": v(31.85, -5.28) * mm, "end": v(32.32, -5.62) * mm});
            skLineSegment(sketch, "E17.43.5", {"start": v(30.31, -4.8) * mm, "end": v(31.36, -4.97) * mm});
            skLineSegment(sketch, "E17.44.0", {"start": v(30.52, -3.2) * mm, "end": v(31.58, -3.32) * mm});
            skArc(sketch, "E17.44.1", {"start": v(31.58, -3.32) * mm, "mid": v(32.13, -3.15) * mm, "end": v(32.67, -2.94) * mm});
            skArc(sketch, "E17.44.2", {"start": v(32.67, -2.94) * mm, "mid": v(32.69, -2.76) * mm, "end": v(32.7, -2.57) * mm});
            skArc(sketch, "E17.44.3", {"start": v(32.73, -2.21) * mm, "mid": v(32.72, -2.4) * mm, "end": v(32.7, -2.57) * mm});
            skArc(sketch, "E17.44.4", {"start": v(31.7, -1.66) * mm, "mid": v(32.23, -1.92) * mm, "end": v(32.73, -2.21) * mm});
            skLineSegment(sketch, "E17.44.5", {"start": v(30.65, -1.6) * mm, "end": v(31.7, -1.66) * mm});
            skLineSegment(sketch, "E17.45.0", {"start": v(30.7, 0) * mm, "end": v(31.75, 0) * mm});
            skArc(sketch, "E17.45.1", {"start": v(31.75, 0) * mm, "mid": v(32.28, 0.23) * mm, "end": v(32.8, 0.5) * mm});
            skArc(sketch, "E17.45.2", {"start": v(32.8, 0.5) * mm, "mid": v(32.8, 0.68) * mm, "end": v(32.8, 0.86) * mm});
            skArc(sketch, "E17.45.3", {"start": v(32.78, 1.22) * mm, "mid": v(32.79, 1.04) * mm, "end": v(32.8, 0.86) * mm});
            skArc(sketch, "E17.45.4", {"start": v(31.7, 1.66) * mm, "mid": v(32.25, 1.46) * mm, "end": v(32.78, 1.22) * mm});
            skLineSegment(sketch, "E17.45.5", {"start": v(30.65, 1.6) * mm, "end": v(31.7, 1.66) * mm});
            skLineSegment(sketch, "E17.46.0", {"start": v(30.52, 3.2) * mm, "end": v(31.58, 3.32) * mm});
            skArc(sketch, "E17.46.1", {"start": v(31.58, 3.32) * mm, "mid": v(32.08, 3.6) * mm, "end": v(32.57, 3.92) * mm});
            skArc(sketch, "E17.46.2", {"start": v(32.57, 3.92) * mm, "mid": v(32.55, 4.1) * mm, "end": v(32.52, 4.28) * mm});
            skArc(sketch, "E17.46.3", {"start": v(32.47, 4.64) * mm, "mid": v(32.5, 4.46) * mm, "end": v(32.52, 4.28) * mm});
            skArc(sketch, "E17.46.4", {"start": v(31.36, 4.97) * mm, "mid": v(31.92, 4.82) * mm, "end": v(32.47, 4.64) * mm});
            skLineSegment(sketch, "E17.46.5", {"start": v(30.31, 4.8) * mm, "end": v(31.36, 4.97) * mm});
            skLineSegment(sketch, "E17.47.0", {"start": v(30.02, 6.38) * mm, "end": v(31.06, 6.6) * mm});
            skArc(sketch, "E17.47.1", {"start": v(31.06, 6.6) * mm, "mid": v(31.53, 6.94) * mm, "end": v(31.98, 7.3) * mm});
            skArc(sketch, "E17.47.2", {"start": v(31.98, 7.3) * mm, "mid": v(31.94, 7.48) * mm, "end": v(31.9, 7.66) * mm});
            skArc(sketch, "E17.47.3", {"start": v(31.81, 8.01) * mm, "mid": v(31.85, 7.83) * mm, "end": v(31.9, 7.66) * mm});
            skArc(sketch, "E17.47.4", {"start": v(30.67, 8.22) * mm, "mid": v(31.24, 8.14) * mm, "end": v(31.81, 8.01) * mm});
            skLineSegment(sketch, "E17.47.5", {"start": v(29.65, 7.94) * mm, "end": v(30.67, 8.22) * mm});
            skLineSegment(sketch, "E17.48.0", {"start": v(29.19, 9.48) * mm, "end": v(30.2, 9.81) * mm});
            skArc(sketch, "E17.48.1", {"start": v(30.2, 9.81) * mm, "mid": v(30.63, 10.2) * mm, "end": v(31.04, 10.6) * mm});
            skArc(sketch, "E17.48.2", {"start": v(31.04, 10.6) * mm, "mid": v(30.98, 10.78) * mm, "end": v(30.92, 10.95) * mm});
            skArc(sketch, "E17.48.3", {"start": v(30.8, 11.3) * mm, "mid": v(30.86, 11.12) * mm, "end": v(30.92, 10.95) * mm});
            skArc(sketch, "E17.48.4", {"start": v(29.64, 11.38) * mm, "mid": v(30.22, 11.36) * mm, "end": v(30.8, 11.3) * mm});
            skLineSegment(sketch, "E17.48.5", {"start": v(28.65, 11) * mm, "end": v(29.64, 11.38) * mm});
            skLineSegment(sketch, "E17.49.0", {"start": v(28.04, 12.48) * mm, "end": v(29, 12.91) * mm});
            skArc(sketch, "E17.49.1", {"start": v(29, 12.91) * mm, "mid": v(29.4, 13.34) * mm, "end": v(29.76, 13.8) * mm});
            skArc(sketch, "E17.49.2", {"start": v(29.76, 13.8) * mm, "mid": v(29.69, 13.96) * mm, "end": v(29.6, 14.12) * mm});
            skArc(sketch, "E17.49.3", {"start": v(29.45, 14.45) * mm, "mid": v(29.53, 14.29) * mm, "end": v(29.6, 14.12) * mm});
            skArc(sketch, "E17.49.4", {"start": v(28.29, 14.41) * mm, "mid": v(28.87, 14.45) * mm, "end": v(29.45, 14.45) * mm});
            skLineSegment(sketch, "E17.49.5", {"start": v(27.35, 13.93) * mm, "end": v(28.29, 14.41) * mm});
            skLineSegment(sketch, "E17.50.0", {"start": v(26.58, 15.35) * mm, "end": v(27.5, 15.88) * mm});
            skArc(sketch, "E17.50.1", {"start": v(27.5, 15.88) * mm, "mid": v(27.84, 16.34) * mm, "end": v(28.16, 16.83) * mm});
            skArc(sketch, "E17.50.2", {"start": v(28.16, 16.83) * mm, "mid": v(28.06, 16.98) * mm, "end": v(27.97, 17.14) * mm});
            skArc(sketch, "E17.50.3", {"start": v(27.78, 17.45) * mm, "mid": v(27.87, 17.3) * mm, "end": v(27.97, 17.14) * mm});
            skArc(sketch, "E17.50.4", {"start": v(26.63, 17.3) * mm, "mid": v(27.2, 17.4) * mm, "end": v(27.78, 17.45) * mm});
            skLineSegment(sketch, "E17.50.5", {"start": v(25.74, 16.72) * mm, "end": v(26.63, 17.3) * mm});
            skLineSegment(sketch, "E17.51.0", {"start": v(24.83, 18.04) * mm, "end": v(25.69, 18.66) * mm});
            skArc(sketch, "E17.51.1", {"start": v(25.69, 18.66) * mm, "mid": v(25.98, 19.16) * mm, "end": v(26.25, 19.68) * mm});
            skArc(sketch, "E17.51.2", {"start": v(26.25, 19.68) * mm, "mid": v(26.14, 19.83) * mm, "end": v(26.03, 19.97) * mm});
            skArc(sketch, "E17.51.3", {"start": v(25.8, 20.26) * mm, "mid": v(25.91, 20.11) * mm, "end": v(26.03, 19.97) * mm});
            skArc(sketch, "E17.51.4", {"start": v(24.67, 19.98) * mm, "mid": v(25.23, 20.14) * mm, "end": v(25.8, 20.26) * mm});
            skLineSegment(sketch, "E17.51.5", {"start": v(23.85, 19.31) * mm, "end": v(24.67, 19.98) * mm});
            skLineSegment(sketch, "E17.52.0", {"start": v(22.8, 20.54) * mm, "end": v(23.6, 21.24) * mm});
            skArc(sketch, "E17.52.1", {"start": v(23.6, 21.24) * mm, "mid": v(23.84, 21.77) * mm, "end": v(24.04, 22.32) * mm});
            skArc(sketch, "E17.52.2", {"start": v(24.04, 22.32) * mm, "mid": v(23.92, 22.45) * mm, "end": v(23.8, 22.58) * mm});
            skArc(sketch, "E17.52.3", {"start": v(23.54, 22.84) * mm, "mid": v(23.67, 22.71) * mm, "end": v(23.8, 22.58) * mm});
            skArc(sketch, "E17.52.4", {"start": v(22.45, 22.45) * mm, "mid": v(22.99, 22.67) * mm, "end": v(23.54, 22.84) * mm});
            skLineSegment(sketch, "E17.52.5", {"start": v(21.7, 21.7) * mm, "end": v(22.45, 22.45) * mm});
            skLineSegment(sketch, "E17.53.0", {"start": v(20.54, 22.8) * mm, "end": v(21.24, 23.6) * mm});
            skArc(sketch, "E17.53.1", {"start": v(21.24, 23.6) * mm, "mid": v(21.43, 24.14) * mm, "end": v(21.58, 24.7) * mm});
            skArc(sketch, "E17.53.2", {"start": v(21.58, 24.7) * mm, "mid": v(21.44, 24.83) * mm, "end": v(21.3, 24.94) * mm});
            skArc(sketch, "E17.53.3", {"start": v(21.03, 25.18) * mm, "mid": v(21.17, 25.06) * mm, "end": v(21.3, 24.94) * mm});
            skArc(sketch, "E17.53.4", {"start": v(19.98, 24.67) * mm, "mid": v(20.5, 24.95) * mm, "end": v(21.03, 25.18) * mm});
            skLineSegment(sketch, "E17.53.5", {"start": v(19.31, 23.85) * mm, "end": v(19.98, 24.67) * mm});
            skLineSegment(sketch, "E17.54.0", {"start": v(18.04, 24.83) * mm, "end": v(18.66, 25.69) * mm});
            skArc(sketch, "E17.54.1", {"start": v(18.66, 25.69) * mm, "mid": v(18.8, 26.25) * mm, "end": v(18.88, 26.83) * mm});
            skArc(sketch, "E17.54.2", {"start": v(18.88, 26.83) * mm, "mid": v(18.73, 26.93) * mm, "end": v(18.58, 27.03) * mm});
            skArc(sketch, "E17.54.3", {"start": v(18.28, 27.24) * mm, "mid": v(18.43, 27.14) * mm, "end": v(18.58, 27.03) * mm});
            skArc(sketch, "E17.54.4", {"start": v(17.3, 26.63) * mm, "mid": v(17.77, 26.95) * mm, "end": v(18.28, 27.24) * mm});
            skLineSegment(sketch, "E17.54.5", {"start": v(16.72, 25.74) * mm, "end": v(17.3, 26.63) * mm});
            skLineSegment(sketch, "E17.55.0", {"start": v(15.35, 26.58) * mm, "end": v(15.87, 27.5) * mm});
            skArc(sketch, "E17.55.1", {"start": v(15.87, 27.5) * mm, "mid": v(15.94, 28.07) * mm, "end": v(15.97, 28.65) * mm});
            skArc(sketch, "E17.55.2", {"start": v(15.97, 28.65) * mm, "mid": v(15.81, 28.74) * mm, "end": v(15.65, 28.83) * mm});
            skArc(sketch, "E17.55.3", {"start": v(15.33, 29) * mm, "mid": v(15.5, 28.92) * mm, "end": v(15.65, 28.83) * mm});
            skArc(sketch, "E17.55.4", {"start": v(14.41, 28.29) * mm, "mid": v(14.86, 28.66) * mm, "end": v(15.33, 29) * mm});
            skLineSegment(sketch, "E17.55.5", {"start": v(13.93, 27.35) * mm, "end": v(14.41, 28.29) * mm});
            skLineSegment(sketch, "E17.56.0", {"start": v(12.48, 28.04) * mm, "end": v(12.91, 29) * mm});
            skArc(sketch, "E17.56.1", {"start": v(12.91, 29) * mm, "mid": v(12.92, 29.59) * mm, "end": v(12.89, 30.17) * mm});
            skArc(sketch, "E17.56.2", {"start": v(12.89, 30.17) * mm, "mid": v(12.72, 30.24) * mm, "end": v(12.55, 30.3) * mm});
            skArc(sketch, "E17.56.3", {"start": v(12.22, 30.44) * mm, "mid": v(12.39, 30.38) * mm, "end": v(12.55, 30.3) * mm});
            skArc(sketch, "E17.56.4", {"start": v(11.38, 29.64) * mm, "mid": v(11.78, 30.06) * mm, "end": v(12.22, 30.44) * mm});
            skLineSegment(sketch, "E17.56.5", {"start": v(11, 28.65) * mm, "end": v(11.38, 29.64) * mm});
            skLineSegment(sketch, "E17.57.0", {"start": v(9.48, 29.19) * mm, "end": v(9.81, 30.2) * mm});
            skArc(sketch, "E17.57.1", {"start": v(9.81, 30.2) * mm, "mid": v(9.76, 30.77) * mm, "end": v(9.67, 31.35) * mm});
            skArc(sketch, "E17.57.2", {"start": v(9.67, 31.35) * mm, "mid": v(9.5, 31.4) * mm, "end": v(9.32, 31.45) * mm});
            skArc(sketch, "E17.57.3", {"start": v(8.97, 31.55) * mm, "mid": v(9.14, 31.5) * mm, "end": v(9.32, 31.45) * mm});
            skArc(sketch, "E17.57.4", {"start": v(8.22, 30.67) * mm, "mid": v(8.58, 31.13) * mm, "end": v(8.97, 31.55) * mm});
            skLineSegment(sketch, "E17.57.5", {"start": v(7.94, 29.65) * mm, "end": v(8.22, 30.67) * mm});
            skLineSegment(sketch, "E17.58.0", {"start": v(6.38, 30.02) * mm, "end": v(6.6, 31.06) * mm});
            skArc(sketch, "E17.58.1", {"start": v(6.6, 31.06) * mm, "mid": v(6.49, 31.63) * mm, "end": v(6.34, 32.19) * mm});
            skArc(sketch, "E17.58.2", {"start": v(6.34, 32.19) * mm, "mid": v(6.16, 32.22) * mm, "end": v(5.98, 32.25) * mm});
            skArc(sketch, "E17.58.3", {"start": v(5.62, 32.32) * mm, "mid": v(5.8, 32.29) * mm, "end": v(5.98, 32.25) * mm});
            skArc(sketch, "E17.58.4", {"start": v(4.97, 31.36) * mm, "mid": v(5.28, 31.85) * mm, "end": v(5.62, 32.32) * mm});
            skLineSegment(sketch, "E17.58.5", {"start": v(4.8, 30.31) * mm, "end": v(4.97, 31.36) * mm});
            skLineSegment(sketch, "E17.59.0", {"start": v(3.2, 30.52) * mm, "end": v(3.32, 31.58) * mm});
            skArc(sketch, "E17.59.1", {"start": v(3.32, 31.58) * mm, "mid": v(3.15, 32.13) * mm, "end": v(2.94, 32.67) * mm});
            skArc(sketch, "E17.59.2", {"start": v(2.94, 32.67) * mm, "mid": v(2.76, 32.69) * mm, "end": v(2.57, 32.7) * mm});
            skArc(sketch, "E17.59.3", {"start": v(2.21, 32.73) * mm, "mid": v(2.4, 32.72) * mm, "end": v(2.57, 32.7) * mm});
            skArc(sketch, "E17.59.4", {"start": v(1.66, 31.7) * mm, "mid": v(1.92, 32.23) * mm, "end": v(2.21, 32.73) * mm});
            skLineSegment(sketch, "E17.59.5", {"start": v(1.6, 30.65) * mm, "end": v(1.66, 31.7) * mm});
            skSolve(sketch);
        }
        {
            var Q0;
            Q0 = qSketchRegion(id + "F0", true);
            extrude(context, id + "F1", {"entities" : qUnion([Q0]), "depth" : 25.4 * mm});
        }
        {
            var Q0;
            Q0 = qSketchRegion(id + "F0", true);
            extrude(context, id + "F2", {"entities" : qUnion([Q0]), "operationType" : NewBodyOperationType.ADD, "depth" : 25.4 * mm});
        }
        {
            var Q0;
            Q0=makeQuery(id+"F1.opExtrude","CAP_FACE",FACE,{"disambiguationData":[OSD([sQuery(id+"F0.wireOp",EDGE,"E0"),sQuery(id+"F0.wireOp",EDGE,"E1"),sQuery(id+"F0.wireOp",EDGE,"E2"),sQuery(id+"F0.wireOp",EDGE,"E3"),sQuery(id+"F0.wireOp",EDGE,"E5.trimOffspring"),sQuery(id+"F0.wireOp",EDGE,"E7.trimOffspring"),sQuery(id+"F0.wireOp",EDGE,"E8.trimOffspring"),sQuery(id+"F0.wireOp",EDGE,"E9.trimOffspring"),sQuery(id+"F0.wireOp",EDGE,"E12"),sQuery(id+"F0.wireOp",EDGE,"E14.MirrorCS"),sQuery(id+"F0.wireOp",EDGE,"E15.MirrorCS"),sQuery(id+"F0.wireOp",EDGE,"E16.MirrorCS"),sQuery(id+"F0.wireOp",EDGE,"E17.1.0"),sQuery(id+"F0.wireOp",EDGE,"E17.1.1"),sQuery(id+"F0.wireOp",EDGE,"E17.1.2"),sQuery(id+"F0.wireOp",EDGE,"E17.1.3"),sQuery(id+"F0.wireOp",EDGE,"E17.1.4"),sQuery(id+"F0.wireOp",EDGE,"E17.1.5"),sQuery(id+"F0.wireOp",EDGE,"E17.2.0"),sQuery(id+"F0.wireOp",EDGE,"E17.2.1"),sQuery(id+"F0.wireOp",EDGE,"E17.2.2"),sQuery(id+"F0.wireOp",EDGE,"E17.2.3"),sQuery(id+"F0.wireOp",EDGE,"E17.2.4"),sQuery(id+"F0.wireOp",EDGE,"E17.2.5"),sQuery(id+"F0.wireOp",EDGE,"E17.3.0"),sQuery(id+"F0.wireOp",EDGE,"E17.3.1"),sQuery(id+"F0.wireOp",EDGE,"E17.3.2"),sQuery(id+"F0.wireOp",EDGE,"E17.3.3"),sQuery(id+"F0.wireOp",EDGE,"E17.3.4"),sQuery(id+"F0.wireOp",EDGE,"E17.3.5"),sQuery(id+"F0.wireOp",EDGE,"E17.4.0"),sQuery(id+"F0.wireOp",EDGE,"E17.4.1"),sQuery(id+"F0.wireOp",EDGE,"E17.4.2"),sQuery(id+"F0.wireOp",EDGE,"E17.4.3"),sQuery(id+"F0.wireOp",EDGE,"E17.4.4"),sQuery(id+"F0.wireOp",EDGE,"E17.4.5"),sQuery(id+"F0.wireOp",EDGE,"E17.5.0"),sQuery(id+"F0.wireOp",EDGE,"E17.5.1"),sQuery(id+"F0.wireOp",EDGE,"E17.5.2"),sQuery(id+"F0.wireOp",EDGE,"E17.5.3"),sQuery(id+"F0.wireOp",EDGE,"E17.5.4"),sQuery(id+"F0.wireOp",EDGE,"E17.5.5"),sQuery(id+"F0.wireOp",EDGE,"E17.6.0"),sQuery(id+"F0.wireOp",EDGE,"E17.6.1"),sQuery(id+"F0.wireOp",EDGE,"E17.6.2"),sQuery(id+"F0.wireOp",EDGE,"E17.6.3"),sQuery(id+"F0.wireOp",EDGE,"E17.6.4"),sQuery(id+"F0.wireOp",EDGE,"E17.6.5"),sQuery(id+"F0.wireOp",EDGE,"E17.7.0"),sQuery(id+"F0.wireOp",EDGE,"E17.7.1"),sQuery(id+"F0.wireOp",EDGE,"E17.7.2"),sQuery(id+"F0.wireOp",EDGE,"E17.7.3"),sQuery(id+"F0.wireOp",EDGE,"E17.7.4"),sQuery(id+"F0.wireOp",EDGE,"E17.7.5"),sQuery(id+"F0.wireOp",EDGE,"E17.8.0"),sQuery(id+"F0.wireOp",EDGE,"E17.8.1"),sQuery(id+"F0.wireOp",EDGE,"E17.8.2"),sQuery(id+"F0.wireOp",EDGE,"E17.8.3"),sQuery(id+"F0.wireOp",EDGE,"E17.8.4"),sQuery(id+"F0.wireOp",EDGE,"E17.8.5"),sQuery(id+"F0.wireOp",EDGE,"E17.9.0"),sQuery(id+"F0.wireOp",EDGE,"E17.9.1"),sQuery(id+"F0.wireOp",EDGE,"E17.9.2"),sQuery(id+"F0.wireOp",EDGE,"E17.9.3"),sQuery(id+"F0.wireOp",EDGE,"E17.9.4"),sQuery(id+"F0.wireOp",EDGE,"E17.9.5"),sQuery(id+"F0.wireOp",EDGE,"E17.10.0"),sQuery(id+"F0.wireOp",EDGE,"E17.10.1"),sQuery(id+"F0.wireOp",EDGE,"E17.10.2"),sQuery(id+"F0.wireOp",EDGE,"E17.10.3"),sQuery(id+"F0.wireOp",EDGE,"E17.10.4"),sQuery(id+"F0.wireOp",EDGE,"E17.10.5"),sQuery(id+"F0.wireOp",EDGE,"E17.11.0"),sQuery(id+"F0.wireOp",EDGE,"E17.11.1"),sQuery(id+"F0.wireOp",EDGE,"E17.11.2"),sQuery(id+"F0.wireOp",EDGE,"E17.11.3"),sQuery(id+"F0.wireOp",EDGE,"E17.11.4"),sQuery(id+"F0.wireOp",EDGE,"E17.11.5"),sQuery(id+"F0.wireOp",EDGE,"E17.12.0"),sQuery(id+"F0.wireOp",EDGE,"E17.12.1"),sQuery(id+"F0.wireOp",EDGE,"E17.12.2"),sQuery(id+"F0.wireOp",EDGE,"E17.12.3"),sQuery(id+"F0.wireOp",EDGE,"E17.12.4"),sQuery(id+"F0.wireOp",EDGE,"E17.12.5"),sQuery(id+"F0.wireOp",EDGE,"E17.13.0"),sQuery(id+"F0.wireOp",EDGE,"E17.13.1"),sQuery(id+"F0.wireOp",EDGE,"E17.13.2"),sQuery(id+"F0.wireOp",EDGE,"E17.13.3"),sQuery(id+"F0.wireOp",EDGE,"E17.13.4"),sQuery(id+"F0.wireOp",EDGE,"E17.13.5"),sQuery(id+"F0.wireOp",EDGE,"E17.14.0"),sQuery(id+"F0.wireOp",EDGE,"E17.14.1"),sQuery(id+"F0.wireOp",EDGE,"E17.14.2"),sQuery(id+"F0.wireOp",EDGE,"E17.14.3"),sQuery(id+"F0.wireOp",EDGE,"E17.14.4"),sQuery(id+"F0.wireOp",EDGE,"E17.14.5"),sQuery(id+"F0.wireOp",EDGE,"E17.15.0"),sQuery(id+"F0.wireOp",EDGE,"E17.15.1"),sQuery(id+"F0.wireOp",EDGE,"E17.15.2"),sQuery(id+"F0.wireOp",EDGE,"E17.15.3"),sQuery(id+"F0.wireOp",EDGE,"E17.15.4"),sQuery(id+"F0.wireOp",EDGE,"E17.15.5"),sQuery(id+"F0.wireOp",EDGE,"E17.16.0"),sQuery(id+"F0.wireOp",EDGE,"E17.16.1"),sQuery(id+"F0.wireOp",EDGE,"E17.16.2"),sQuery(id+"F0.wireOp",EDGE,"E17.16.3"),sQuery(id+"F0.wireOp",EDGE,"E17.16.4"),sQuery(id+"F0.wireOp",EDGE,"E17.16.5"),sQuery(id+"F0.wireOp",EDGE,"E17.17.0"),sQuery(id+"F0.wireOp",EDGE,"E17.17.1"),sQuery(id+"F0.wireOp",EDGE,"E17.17.2"),sQuery(id+"F0.wireOp",EDGE,"E17.17.3"),sQuery(id+"F0.wireOp",EDGE,"E17.17.4"),sQuery(id+"F0.wireOp",EDGE,"E17.17.5"),sQuery(id+"F0.wireOp",EDGE,"E17.18.0"),sQuery(id+"F0.wireOp",EDGE,"E17.18.1"),sQuery(id+"F0.wireOp",EDGE,"E17.18.2"),sQuery(id+"F0.wireOp",EDGE,"E17.18.3"),sQuery(id+"F0.wireOp",EDGE,"E17.18.4"),sQuery(id+"F0.wireOp",EDGE,"E17.18.5"),sQuery(id+"F0.wireOp",EDGE,"E17.19.0"),sQuery(id+"F0.wireOp",EDGE,"E17.19.1"),sQuery(id+"F0.wireOp",EDGE,"E17.19.2"),sQuery(id+"F0.wireOp",EDGE,"E17.19.3"),sQuery(id+"F0.wireOp",EDGE,"E17.19.4"),sQuery(id+"F0.wireOp",EDGE,"E17.19.5"),sQuery(id+"F0.wireOp",EDGE,"E17.20.0"),sQuery(id+"F0.wireOp",EDGE,"E17.20.1"),sQuery(id+"F0.wireOp",EDGE,"E17.20.2"),sQuery(id+"F0.wireOp",EDGE,"E17.20.3"),sQuery(id+"F0.wireOp",EDGE,"E17.20.4"),sQuery(id+"F0.wireOp",EDGE,"E17.20.5"),sQuery(id+"F0.wireOp",EDGE,"E17.21.0"),sQuery(id+"F0.wireOp",EDGE,"E17.21.1"),sQuery(id+"F0.wireOp",EDGE,"E17.21.2"),sQuery(id+"F0.wireOp",EDGE,"E17.21.3"),sQuery(id+"F0.wireOp",EDGE,"E17.21.4"),sQuery(id+"F0.wireOp",EDGE,"E17.21.5"),sQuery(id+"F0.wireOp",EDGE,"E17.22.0"),sQuery(id+"F0.wireOp",EDGE,"E17.22.1"),sQuery(id+"F0.wireOp",EDGE,"E17.22.2"),sQuery(id+"F0.wireOp",EDGE,"E17.22.3"),sQuery(id+"F0.wireOp",EDGE,"E17.22.4"),sQuery(id+"F0.wireOp",EDGE,"E17.22.5"),sQuery(id+"F0.wireOp",EDGE,"E17.23.0"),sQuery(id+"F0.wireOp",EDGE,"E17.23.1"),sQuery(id+"F0.wireOp",EDGE,"E17.23.2"),sQuery(id+"F0.wireOp",EDGE,"E17.23.3"),sQuery(id+"F0.wireOp",EDGE,"E17.23.4"),sQuery(id+"F0.wireOp",EDGE,"E17.23.5"),sQuery(id+"F0.wireOp",EDGE,"E17.24.0"),sQuery(id+"F0.wireOp",EDGE,"E17.24.1"),sQuery(id+"F0.wireOp",EDGE,"E17.24.2"),sQuery(id+"F0.wireOp",EDGE,"E17.24.3"),sQuery(id+"F0.wireOp",EDGE,"E17.24.4"),sQuery(id+"F0.wireOp",EDGE,"E17.24.5"),sQuery(id+"F0.wireOp",EDGE,"E17.25.0"),sQuery(id+"F0.wireOp",EDGE,"E17.25.1"),sQuery(id+"F0.wireOp",EDGE,"E17.25.2"),sQuery(id+"F0.wireOp",EDGE,"E17.25.3"),sQuery(id+"F0.wireOp",EDGE,"E17.25.4"),sQuery(id+"F0.wireOp",EDGE,"E17.25.5"),sQuery(id+"F0.wireOp",EDGE,"E17.26.0"),sQuery(id+"F0.wireOp",EDGE,"E17.26.1"),sQuery(id+"F0.wireOp",EDGE,"E17.26.2"),sQuery(id+"F0.wireOp",EDGE,"E17.26.3"),sQuery(id+"F0.wireOp",EDGE,"E17.26.4"),sQuery(id+"F0.wireOp",EDGE,"E17.26.5"),sQuery(id+"F0.wireOp",EDGE,"E17.27.0"),sQuery(id+"F0.wireOp",EDGE,"E17.27.1"),sQuery(id+"F0.wireOp",EDGE,"E17.27.2"),sQuery(id+"F0.wireOp",EDGE,"E17.27.3"),sQuery(id+"F0.wireOp",EDGE,"E17.27.4"),sQuery(id+"F0.wireOp",EDGE,"E17.27.5"),sQuery(id+"F0.wireOp",EDGE,"E17.28.0"),sQuery(id+"F0.wireOp",EDGE,"E17.28.1"),sQuery(id+"F0.wireOp",EDGE,"E17.28.2"),sQuery(id+"F0.wireOp",EDGE,"E17.28.3"),sQuery(id+"F0.wireOp",EDGE,"E17.28.4"),sQuery(id+"F0.wireOp",EDGE,"E17.28.5"),sQuery(id+"F0.wireOp",EDGE,"E17.29.0"),sQuery(id+"F0.wireOp",EDGE,"E17.29.1"),sQuery(id+"F0.wireOp",EDGE,"E17.29.2"),sQuery(id+"F0.wireOp",EDGE,"E17.29.3"),sQuery(id+"F0.wireOp",EDGE,"E17.29.4"),sQuery(id+"F0.wireOp",EDGE,"E17.29.5"),sQuery(id+"F0.wireOp",EDGE,"E17.30.0"),sQuery(id+"F0.wireOp",EDGE,"E17.30.1"),sQuery(id+"F0.wireOp",EDGE,"E17.30.2"),sQuery(id+"F0.wireOp",EDGE,"E17.30.3"),sQuery(id+"F0.wireOp",EDGE,"E17.30.4"),sQuery(id+"F0.wireOp",EDGE,"E17.30.5"),sQuery(id+"F0.wireOp",EDGE,"E17.31.0"),sQuery(id+"F0.wireOp",EDGE,"E17.31.1"),sQuery(id+"F0.wireOp",EDGE,"E17.31.2"),sQuery(id+"F0.wireOp",EDGE,"E17.31.3"),sQuery(id+"F0.wireOp",EDGE,"E17.31.4"),sQuery(id+"F0.wireOp",EDGE,"E17.31.5"),sQuery(id+"F0.wireOp",EDGE,"E17.32.0"),sQuery(id+"F0.wireOp",EDGE,"E17.32.1"),sQuery(id+"F0.wireOp",EDGE,"E17.32.2"),sQuery(id+"F0.wireOp",EDGE,"E17.32.3"),sQuery(id+"F0.wireOp",EDGE,"E17.32.4"),sQuery(id+"F0.wireOp",EDGE,"E17.32.5"),sQuery(id+"F0.wireOp",EDGE,"E17.33.0"),sQuery(id+"F0.wireOp",EDGE,"E17.33.1"),sQuery(id+"F0.wireOp",EDGE,"E17.33.2"),sQuery(id+"F0.wireOp",EDGE,"E17.33.3"),sQuery(id+"F0.wireOp",EDGE,"E17.33.4"),sQuery(id+"F0.wireOp",EDGE,"E17.33.5"),sQuery(id+"F0.wireOp",EDGE,"E17.34.0"),sQuery(id+"F0.wireOp",EDGE,"E17.34.1"),sQuery(id+"F0.wireOp",EDGE,"E17.34.2"),sQuery(id+"F0.wireOp",EDGE,"E17.34.3"),sQuery(id+"F0.wireOp",EDGE,"E17.34.4"),sQuery(id+"F0.wireOp",EDGE,"E17.34.5"),sQuery(id+"F0.wireOp",EDGE,"E17.35.0"),sQuery(id+"F0.wireOp",EDGE,"E17.35.1"),sQuery(id+"F0.wireOp",EDGE,"E17.35.2"),sQuery(id+"F0.wireOp",EDGE,"E17.35.3"),sQuery(id+"F0.wireOp",EDGE,"E17.35.4"),sQuery(id+"F0.wireOp",EDGE,"E17.35.5"),sQuery(id+"F0.wireOp",EDGE,"E17.36.0"),sQuery(id+"F0.wireOp",EDGE,"E17.36.1"),sQuery(id+"F0.wireOp",EDGE,"E17.36.2"),sQuery(id+"F0.wireOp",EDGE,"E17.36.3"),sQuery(id+"F0.wireOp",EDGE,"E17.36.4"),sQuery(id+"F0.wireOp",EDGE,"E17.36.5"),sQuery(id+"F0.wireOp",EDGE,"E17.37.0"),sQuery(id+"F0.wireOp",EDGE,"E17.37.1"),sQuery(id+"F0.wireOp",EDGE,"E17.37.2"),sQuery(id+"F0.wireOp",EDGE,"E17.37.3"),sQuery(id+"F0.wireOp",EDGE,"E17.37.4"),sQuery(id+"F0.wireOp",EDGE,"E17.37.5"),sQuery(id+"F0.wireOp",EDGE,"E17.38.0"),sQuery(id+"F0.wireOp",EDGE,"E17.38.1"),sQuery(id+"F0.wireOp",EDGE,"E17.38.2"),sQuery(id+"F0.wireOp",EDGE,"E17.38.3"),sQuery(id+"F0.wireOp",EDGE,"E17.38.4"),sQuery(id+"F0.wireOp",EDGE,"E17.38.5"),sQuery(id+"F0.wireOp",EDGE,"E17.39.0"),sQuery(id+"F0.wireOp",EDGE,"E17.39.1"),sQuery(id+"F0.wireOp",EDGE,"E17.39.2"),sQuery(id+"F0.wireOp",EDGE,"E17.39.3"),sQuery(id+"F0.wireOp",EDGE,"E17.39.4"),sQuery(id+"F0.wireOp",EDGE,"E17.39.5"),sQuery(id+"F0.wireOp",EDGE,"E17.40.0"),sQuery(id+"F0.wireOp",EDGE,"E17.40.1"),sQuery(id+"F0.wireOp",EDGE,"E17.40.2"),sQuery(id+"F0.wireOp",EDGE,"E17.40.3"),sQuery(id+"F0.wireOp",EDGE,"E17.40.4"),sQuery(id+"F0.wireOp",EDGE,"E17.40.5"),sQuery(id+"F0.wireOp",EDGE,"E17.41.0"),sQuery(id+"F0.wireOp",EDGE,"E17.41.1"),sQuery(id+"F0.wireOp",EDGE,"E17.41.2"),sQuery(id+"F0.wireOp",EDGE,"E17.41.3"),sQuery(id+"F0.wireOp",EDGE,"E17.41.4"),sQuery(id+"F0.wireOp",EDGE,"E17.41.5"),sQuery(id+"F0.wireOp",EDGE,"E17.42.0"),sQuery(id+"F0.wireOp",EDGE,"E17.42.1"),sQuery(id+"F0.wireOp",EDGE,"E17.42.2"),sQuery(id+"F0.wireOp",EDGE,"E17.42.3"),sQuery(id+"F0.wireOp",EDGE,"E17.42.4"),sQuery(id+"F0.wireOp",EDGE,"E17.42.5"),sQuery(id+"F0.wireOp",EDGE,"E17.43.0"),sQuery(id+"F0.wireOp",EDGE,"E17.43.1"),sQuery(id+"F0.wireOp",EDGE,"E17.43.2"),sQuery(id+"F0.wireOp",EDGE,"E17.43.3"),sQuery(id+"F0.wireOp",EDGE,"E17.43.4"),sQuery(id+"F0.wireOp",EDGE,"E17.43.5"),sQuery(id+"F0.wireOp",EDGE,"E17.44.0"),sQuery(id+"F0.wireOp",EDGE,"E17.44.1"),sQuery(id+"F0.wireOp",EDGE,"E17.44.2"),sQuery(id+"F0.wireOp",EDGE,"E17.44.3"),sQuery(id+"F0.wireOp",EDGE,"E17.44.4"),sQuery(id+"F0.wireOp",EDGE,"E17.44.5"),sQuery(id+"F0.wireOp",EDGE,"E17.45.0"),sQuery(id+"F0.wireOp",EDGE,"E17.45.1"),sQuery(id+"F0.wireOp",EDGE,"E17.45.2"),sQuery(id+"F0.wireOp",EDGE,"E17.45.3"),sQuery(id+"F0.wireOp",EDGE,"E17.45.4"),sQuery(id+"F0.wireOp",EDGE,"E17.45.5"),sQuery(id+"F0.wireOp",EDGE,"E17.46.0"),sQuery(id+"F0.wireOp",EDGE,"E17.46.1"),sQuery(id+"F0.wireOp",EDGE,"E17.46.2"),sQuery(id+"F0.wireOp",EDGE,"E17.46.3"),sQuery(id+"F0.wireOp",EDGE,"E17.46.4"),sQuery(id+"F0.wireOp",EDGE,"E17.46.5"),sQuery(id+"F0.wireOp",EDGE,"E17.47.0"),sQuery(id+"F0.wireOp",EDGE,"E17.47.1"),sQuery(id+"F0.wireOp",EDGE,"E17.47.2"),sQuery(id+"F0.wireOp",EDGE,"E17.47.3"),sQuery(id+"F0.wireOp",EDGE,"E17.47.4"),sQuery(id+"F0.wireOp",EDGE,"E17.47.5"),sQuery(id+"F0.wireOp",EDGE,"E17.48.0"),sQuery(id+"F0.wireOp",EDGE,"E17.48.1"),sQuery(id+"F0.wireOp",EDGE,"E17.48.2"),sQuery(id+"F0.wireOp",EDGE,"E17.48.3"),sQuery(id+"F0.wireOp",EDGE,"E17.48.4"),sQuery(id+"F0.wireOp",EDGE,"E17.48.5"),sQuery(id+"F0.wireOp",EDGE,"E17.49.0"),sQuery(id+"F0.wireOp",EDGE,"E17.49.1"),sQuery(id+"F0.wireOp",EDGE,"E17.49.2"),sQuery(id+"F0.wireOp",EDGE,"E17.49.3"),sQuery(id+"F0.wireOp",EDGE,"E17.49.4"),sQuery(id+"F0.wireOp",EDGE,"E17.49.5"),sQuery(id+"F0.wireOp",EDGE,"E17.50.0"),sQuery(id+"F0.wireOp",EDGE,"E17.50.1"),sQuery(id+"F0.wireOp",EDGE,"E17.50.2"),sQuery(id+"F0.wireOp",EDGE,"E17.50.3"),sQuery(id+"F0.wireOp",EDGE,"E17.50.4"),sQuery(id+"F0.wireOp",EDGE,"E17.50.5"),sQuery(id+"F0.wireOp",EDGE,"E17.51.0"),sQuery(id+"F0.wireOp",EDGE,"E17.51.1"),sQuery(id+"F0.wireOp",EDGE,"E17.51.2"),sQuery(id+"F0.wireOp",EDGE,"E17.51.3"),sQuery(id+"F0.wireOp",EDGE,"E17.51.4"),sQuery(id+"F0.wireOp",EDGE,"E17.51.5"),sQuery(id+"F0.wireOp",EDGE,"E17.52.0"),sQuery(id+"F0.wireOp",EDGE,"E17.52.1"),sQuery(id+"F0.wireOp",EDGE,"E17.52.2"),sQuery(id+"F0.wireOp",EDGE,"E17.52.3"),sQuery(id+"F0.wireOp",EDGE,"E17.52.4"),sQuery(id+"F0.wireOp",EDGE,"E17.52.5"),sQuery(id+"F0.wireOp",EDGE,"E17.53.0"),sQuery(id+"F0.wireOp",EDGE,"E17.53.1"),sQuery(id+"F0.wireOp",EDGE,"E17.53.2"),sQuery(id+"F0.wireOp",EDGE,"E17.53.3"),sQuery(id+"F0.wireOp",EDGE,"E17.53.4"),sQuery(id+"F0.wireOp",EDGE,"E17.53.5"),sQuery(id+"F0.wireOp",EDGE,"E17.54.0"),sQuery(id+"F0.wireOp",EDGE,"E17.54.1"),sQuery(id+"F0.wireOp",EDGE,"E17.54.2"),sQuery(id+"F0.wireOp",EDGE,"E17.54.3"),sQuery(id+"F0.wireOp",EDGE,"E17.54.4"),sQuery(id+"F0.wireOp",EDGE,"E17.54.5"),sQuery(id+"F0.wireOp",EDGE,"E17.55.0"),sQuery(id+"F0.wireOp",EDGE,"E17.55.1"),sQuery(id+"F0.wireOp",EDGE,"E17.55.2"),sQuery(id+"F0.wireOp",EDGE,"E17.55.3"),sQuery(id+"F0.wireOp",EDGE,"E17.55.4"),sQuery(id+"F0.wireOp",EDGE,"E17.55.5"),sQuery(id+"F0.wireOp",EDGE,"E17.56.0"),sQuery(id+"F0.wireOp",EDGE,"E17.56.1"),sQuery(id+"F0.wireOp",EDGE,"E17.56.2"),sQuery(id+"F0.wireOp",EDGE,"E17.56.3"),sQuery(id+"F0.wireOp",EDGE,"E17.56.4"),sQuery(id+"F0.wireOp",EDGE,"E17.56.5"),sQuery(id+"F0.wireOp",EDGE,"E17.57.0"),sQuery(id+"F0.wireOp",EDGE,"E17.57.1"),sQuery(id+"F0.wireOp",EDGE,"E17.57.2"),sQuery(id+"F0.wireOp",EDGE,"E17.57.3"),sQuery(id+"F0.wireOp",EDGE,"E17.57.4"),sQuery(id+"F0.wireOp",EDGE,"E17.57.5"),sQuery(id+"F0.wireOp",EDGE,"E17.58.0"),sQuery(id+"F0.wireOp",EDGE,"E17.58.1"),sQuery(id+"F0.wireOp",EDGE,"E17.58.2"),sQuery(id+"F0.wireOp",EDGE,"E17.58.3"),sQuery(id+"F0.wireOp",EDGE,"E17.58.4"),sQuery(id+"F0.wireOp",EDGE,"E17.58.5"),sQuery(id+"F0.wireOp",EDGE,"E17.59.0"),sQuery(id+"F0.wireOp",EDGE,"E17.59.1"),sQuery(id+"F0.wireOp",EDGE,"E17.59.2"),sQuery(id+"F0.wireOp",EDGE,"E17.59.3"),sQuery(id+"F0.wireOp",EDGE,"E17.59.4"),sQuery(id+"F0.wireOp",EDGE,"E17.59.5")])],"isStart":false});
            var sketch = newSketch(context, id + "F3", { "sketchPlane" : qUnion([Q0])});
            skCircle(sketch, "E18", {"center": v(0, 0) * mm, "radius": 11.43 * mm});
            skSolve(sketch);
        }
        {
            var Q0;
            Q0 = qSketchRegion(id + "F3", true);
            extrude(context, id + "F4", {"entities" : qUnion([Q0]), "operationType" : NewBodyOperationType.ADD, "depth" : 7.37 * mm});
        }
        {
            var Q0;
            Q0=makeQuery(id+"F4.opExtrude","CAP_FACE",FACE,{"disambiguationData":[OSD([sQuery(id+"F3.wireOp",EDGE,"E18")])],"isStart":false});
            var sketch = newSketch(context, id + "F5", { "sketchPlane" : qUnion([Q0])});
            skCircle(sketch, "E19.cCircle", {"center": v(0, 0) * mm, "radius": 11.11 * mm, "construction": true});
            skLineSegment(sketch, "E19.0", {"start": v(-3.37, 10.59) * mm, "end": v(7.49, 8.21) * mm});
            skLineSegment(sketch, "E19.1", {"start": v(7.49, 8.21) * mm, "end": v(10.86, -2.38) * mm});
            skLineSegment(sketch, "E19.2", {"start": v(10.86, -2.38) * mm, "end": v(3.37, -10.59) * mm});
            skLineSegment(sketch, "E19.3", {"start": v(3.37, -10.59) * mm, "end": v(-7.49, -8.21) * mm});
            skLineSegment(sketch, "E19.4", {"start": v(-7.49, -8.21) * mm, "end": v(-10.86, 2.38) * mm});
            skLineSegment(sketch, "E19.5", {"start": v(-10.86, 2.38) * mm, "end": v(-3.37, 10.59) * mm});
            skSolve(sketch);
        }
        {
            var Q0;
            Q0 = qSketchRegion(id + "F5", true);
            extrude(context, id + "F6", {"entities" : qUnion([Q0]), "operationType" : NewBodyOperationType.REMOVE, "oppositeDirection" : true, "depth" : 52.58 * mm});
        }
    });
